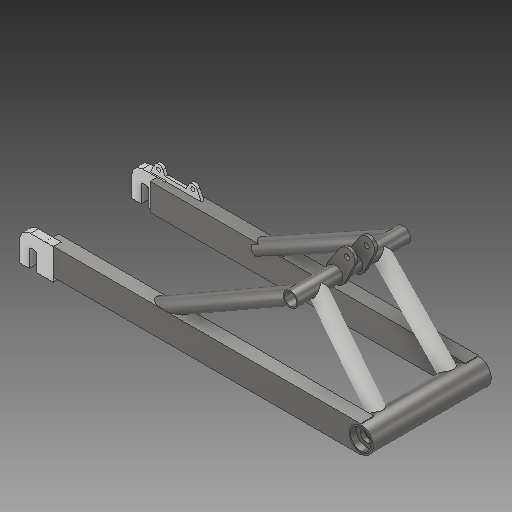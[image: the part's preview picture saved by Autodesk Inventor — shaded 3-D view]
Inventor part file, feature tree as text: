
AUTODESK INVENTOR PART (.ipt)
format: ipt  version: 2019.2 (Build 232265000, 265)  size: 416,256 bytes
history: native  units: mm
features: other x8, extrude x4, sketch x4, plane x3, mirror x2, fillet x1
ambient origin geometry x8: Origin, YZ Plane, XZ Plane, XY Plane, X Axis, Y Axis, Z Axis, Center Point
bodies: Solid5 (feature_tree), Solid6 (feature_tree), Solid1 (feature_tree), Solid2 (feature_tree), Solid3 (feature_tree)
feature tree (22):
  other  "Swingarm.ipt"
  plane  "Work Plane1"
  extrude  "Extrusion1"  [1 undecoded]
  mirror  "Mirror1"
  fillet  "Fillet1"  Radius=16.0mm
  plane  "Work Plane2"
  extrude  "Extrusion2"  Depth=20.0mm
  mirror  "Mirror2"
  extrude  "Extrusion4"  Depth=4.0mm
  plane  "Work Plane4"
  extrude  "Extrusion5"  Depth=10.0mm TaperAngle=0.0deg
  other  "Arms::Swingarm.ipt"
  other  "ShockPlate::Swingarm.ipt"
  other  "PivotCup::Swingarm.ipt"
  other  "TaggingFeature1"
  sketch  "Sketch3"  dims[d0=10.0mm d1=-9.5mm]
  other  "Dropout"
  other  "Pattern of Dropout:1"
  sketch  "Sketch4"  dims[d2=50.0mm d3=27.0mm d4=16.0mm d5=10.0mm d6=12.0mm d7=0.0mm d8=16.0mm]
  sketch  "Sketch5"  dims[d9=25.0mm d10=20.0mm]
  sketch  "Sketch6"  dims[d11=22.225mm d12=2.0mm d13=10.0mm d14=0.0mm d17=10.0mm d18=0.0mm d21=78.1mm d23=39.9mm d24=51.0mm d26=6.0mm d27=6.0mm d28=4.0mm d29=4.0mm d30=4.4mm d31=0.0mm d32=-4.0mm]
  other  "BrakePlate"
note: 1 required parameter value undecoded (feature->parameter linkage not recoverable at this tier; creation-order binding heuristic only, values carry confidence <= 0.55)
